# Revit family: Electronics_Masking-Generators_Biamp_Cambridge_Sound-Masking-Control-Module_QT-X-800_800D___
name_source: partatom
category: Communication Devices
units: mm (PartAtom-declared; Revit-internal decimal feet)

## family parameters
Cut with Voids When Loaded = No
Host = Face
Maintain Annotation Orientation = No
OmniClass Number = 23.85.10.11.11
OmniClass Title = Sound and Signal Devices
Part Type = Normal
Room Calculation Point = No
Round Connector Dimension = Use Diameter
Shared = No

## types (1)
- Qt X 800/800D
    Active Equalization = 125Hz – 8kHz: ISO 1/1 Octave Bands
    Altitude = 0-10,000 ft (0-3000m) MSL
    Apparent Load = 0 VA
    Audio Input Connector Type = Captive Screw Terminal
    Compliance = FCC Part 15B (USA); UL Listed (USA and Canada); CE Marked (Europe); RoHS Directive (Europe)
    Connector Description = PoE (IEEE 802.3at) Connected on Network position 1
    Current = 0 A
    Default Elevation = 48 "
    Depth = 3.8 "
    Description = Cambridge QT X 800/800D Sound Masking Control Module
    Height = 3.5 "
    Housing Material = Biamp - Metal - Black
    Humidity = 0-95% relative humidity (non-condensing)
    Included Accessories = Plenum T-bar mount with wire hanger positions
    Input Gain Range = 6dB steps
    Input Impedance = 8 kohm
    Input Level = +24dBu (12.3VRMS max)
    Input Level Adjustment = 1dB steps
    Manufacturer = Biamp
    Masking Level Adjustment = 0.5dB steps
    Model = Qt X 800/800D
    Nominal Output Impedance = 4 ohm
    Number of Audio Outputs = 8
    Number of Non-Correlated Masking Sources = 8 per zone
    Number of Poles = 1
    Number of Remote Control Outputs = 2 Channels GPIO
    Power Factor = 1
    Product Documentation Link = https://downloads.biamp.com
    Product Page URL = https://www.biamp.com
    Product data url = https://www.bimobject.com
    Remote Control Connector Type = Captive Screw Terminal
    Remote Control Input Type = Contact Closure (Normally Open)
    Remote Control Number of Inputs = 2
    Remote Control Output Type = Logic Status (5VDC)
    Sound Maskin Equalization = 100Hz - 10kHz: ISO 1/3 Octave Bands
    Temperature Range = 40 - 104° F (4 – 40° C)
    URL = https://www.biamp.com
    Voltage = 0 V
    Weight = 2.70 lbf
    Width = 14.63 "

## geometry (parser evidence)
native form markers: Sweep x6
no freeform markers — native parametric forms only
